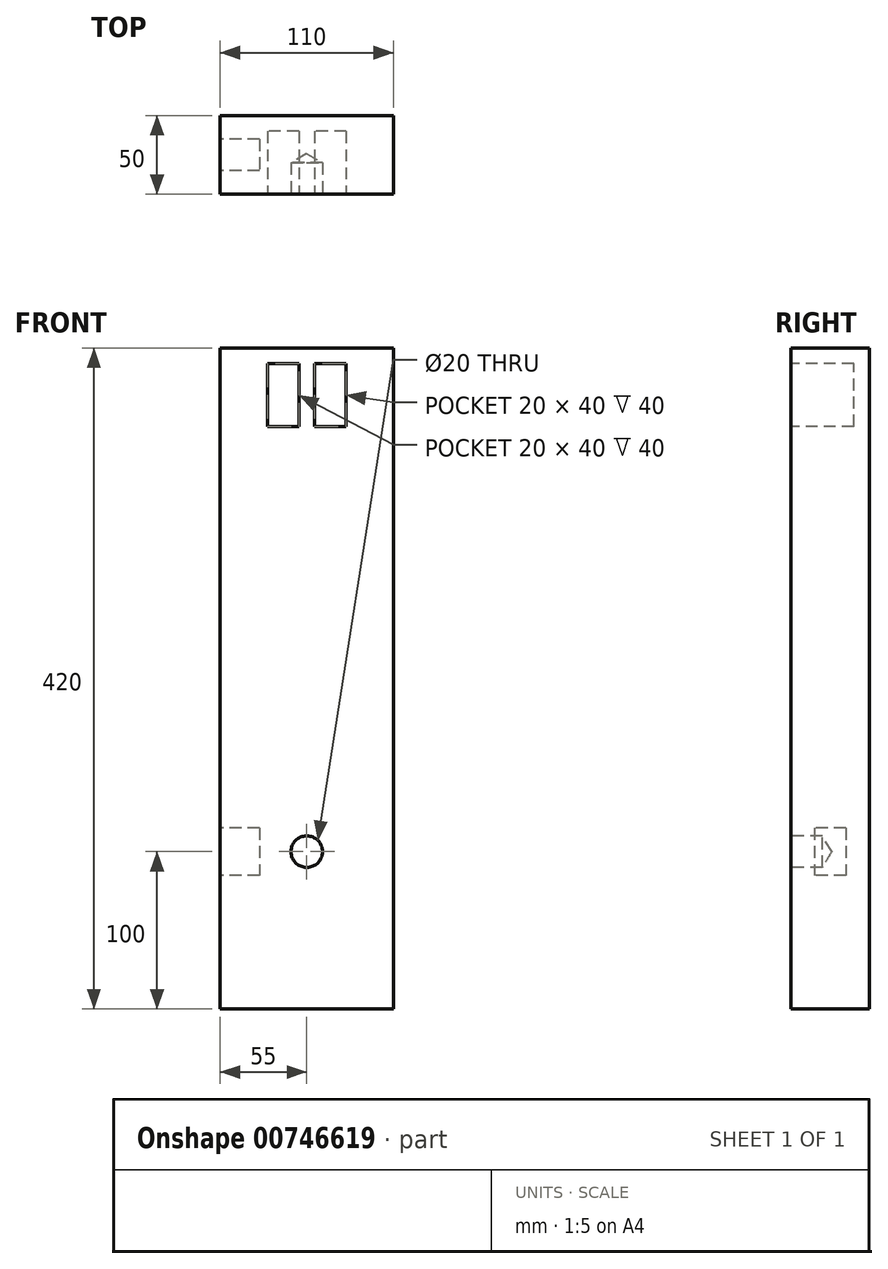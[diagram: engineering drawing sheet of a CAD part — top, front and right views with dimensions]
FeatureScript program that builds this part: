
annotation { "Feature Type Name" : "Feature", "Feature Type Description" : "" }
export const myFeature = defineFeature(function(context is Context, id is Id, definition is map)
    precondition{}
    {
        {
            var Q0;
            Q0=qCreatedBy(makeId("Front.planeOp"),FACE);
            var sketch = newSketch(context, id + "F0", { "sketchPlane" : qUnion([Q0])});
            skLineSegment(sketch, "E0.bottom", {"start": v(55, -210) * mm, "end": v(-55, -210) * mm});
            skLineSegment(sketch, "E0.top", {"start": v(55, 210) * mm, "end": v(-55, 210) * mm});
            skLineSegment(sketch, "E0.left", {"start": v(55, -210) * mm, "end": v(55, 210) * mm});
            skLineSegment(sketch, "E0.right", {"start": v(-55, -210) * mm, "end": v(-55, 210) * mm});
            skPoint(sketch, "E0.middle", {"position": v(0, 0) * mm});
            skSolve(sketch);
        }
        {
            var Q0;
            Q0 = qSketchRegion(id + "F0", true);
            extrude(context, id + "F1", {"entities" : qUnion([Q0]), "oppositeDirection" : true, "depth" : 50 * mm, "offsetDistance" : 25 * mm});
        }
        {
            var Q0;
            Q0=makeQuery(id+"F1.opExtrude","CAP_FACE",FACE,{"disambiguationData":[OSD([sQuery(id+"F0.wireOp",EDGE,"E0.bottom"),sQuery(id+"F0.wireOp",EDGE,"E0.top"),sQuery(id+"F0.wireOp",EDGE,"E0.left"),sQuery(id+"F0.wireOp",EDGE,"E0.right")])],"isStart":true});
            var sketch = newSketch(context, id + "F2", { "sketchPlane" : qUnion([Q0])});
            skPoint(sketch, "E1", {"position": v(0, -110) * mm});
            skPoint(sketch, "E2", {"position": v(-15, 180) * mm});
            skPoint(sketch, "E3", {"position": v(15, 180) * mm});
            skLineSegment(sketch, "E4.bottom", {"start": v(-5, 160) * mm, "end": v(-25, 160) * mm});
            skLineSegment(sketch, "E4.top", {"start": v(-5, 200) * mm, "end": v(-25, 200) * mm});
            skLineSegment(sketch, "E4.left", {"start": v(-5, 160) * mm, "end": v(-5, 200) * mm});
            skLineSegment(sketch, "E4.right", {"start": v(-25, 160) * mm, "end": v(-25, 200) * mm});
            skLineSegment(sketch, "E5.bottom", {"start": v(25, 160) * mm, "end": v(5, 160) * mm});
            skLineSegment(sketch, "E5.top", {"start": v(25, 200) * mm, "end": v(5, 200) * mm});
            skLineSegment(sketch, "E5.left", {"start": v(25, 160) * mm, "end": v(25, 200) * mm});
            skLineSegment(sketch, "E5.right", {"start": v(5, 160) * mm, "end": v(5, 200) * mm});
            skSolve(sketch);
        }
        {
            var Q0;
            Q0=sQuery(id+"F2.wireOp",VERTEX,"E1");
            var Q1;
            Q1=makeQuery(id+"F1.opExtrude","SWEPT_BODY",BODY,{"disambiguationData":[OSD([sQuery(id+"F0.wireOp",EDGE,"E0.bottom"),sQuery(id+"F0.wireOp",EDGE,"E0.top"),sQuery(id+"F0.wireOp",EDGE,"E0.left"),sQuery(id+"F0.wireOp",EDGE,"E0.right")])]});
            hole(context, id + "F3", {"style" : HoleStyle.SIMPLE, "endStyle" : HoleEndStyle.BLIND, "holeDiameter" : 20 * mm, "majorDiameter" : 5 * mm, "holeDepth" : 20 * mm, "isTappedThrough" : true, "tappedDepth" : 12 * mm, "tapClearance" : 3, "locations" : qUnion([Q0]), "scope" : qUnion([Q1])});
        }
        {
            var Q0;
            Q0=makeQuery(id+"F2.imprint","IMPRINT",FACE,{"disambiguationData":[TD([[makeQuery(id+"F2.imprint","IMPRINT",EDGE,{"derivedFrom":sQuery(id+"F2.wireOp",EDGE,"E4.bottom")}),-1.0]])]});
            var Q1;
            Q1=makeQuery(id+"F2.imprint","IMPRINT",FACE,{"disambiguationData":[TD([[makeQuery(id+"F2.imprint","IMPRINT",EDGE,{"derivedFrom":sQuery(id+"F2.wireOp",EDGE,"E5.bottom")}),-1.0]])]});
            extrude(context, id + "F4", {"entities" : qUnion([Q0, Q1]), "operationType" : NewBodyOperationType.REMOVE, "oppositeDirection" : true, "depth" : 40 * mm, "offsetDistance" : 25 * mm});
        }
        {
            var Q0;
            Q0=makeQuery(id+"F1.opExtrude","SWEPT_FACE",FACE,{"disambiguationData":[OSD([sQuery(id+"F0.wireOp",EDGE,"E0.right")])]});
            var sketch = newSketch(context, id + "F5", { "sketchPlane" : qUnion([Q0])});
            skPoint(sketch, "E6", {"position": v(-25, -110) * mm});
            skLineSegment(sketch, "E7.bottom", {"start": v(-35, -95) * mm, "end": v(-15, -95) * mm});
            skLineSegment(sketch, "E7.top", {"start": v(-35, -125) * mm, "end": v(-15, -125) * mm});
            skLineSegment(sketch, "E7.left", {"start": v(-35, -95) * mm, "end": v(-35, -125) * mm});
            skLineSegment(sketch, "E7.right", {"start": v(-15, -95) * mm, "end": v(-15, -125) * mm});
            skSolve(sketch);
        }
        {
            var Q0;
            Q0=makeQuery(id+"F5.imprint","IMPRINT",FACE,{"disambiguationData":[TD([[makeQuery(id+"F5.imprint","IMPRINT",EDGE,{"derivedFrom":sQuery(id+"F5.wireOp",EDGE,"E7.bottom")}),-1.0]])]});
            extrude(context, id + "F6", {"entities" : qUnion([Q0]), "operationType" : NewBodyOperationType.REMOVE, "oppositeDirection" : true, "depth" : 25 * mm, "offsetDistance" : 25 * mm});
        }
    });
